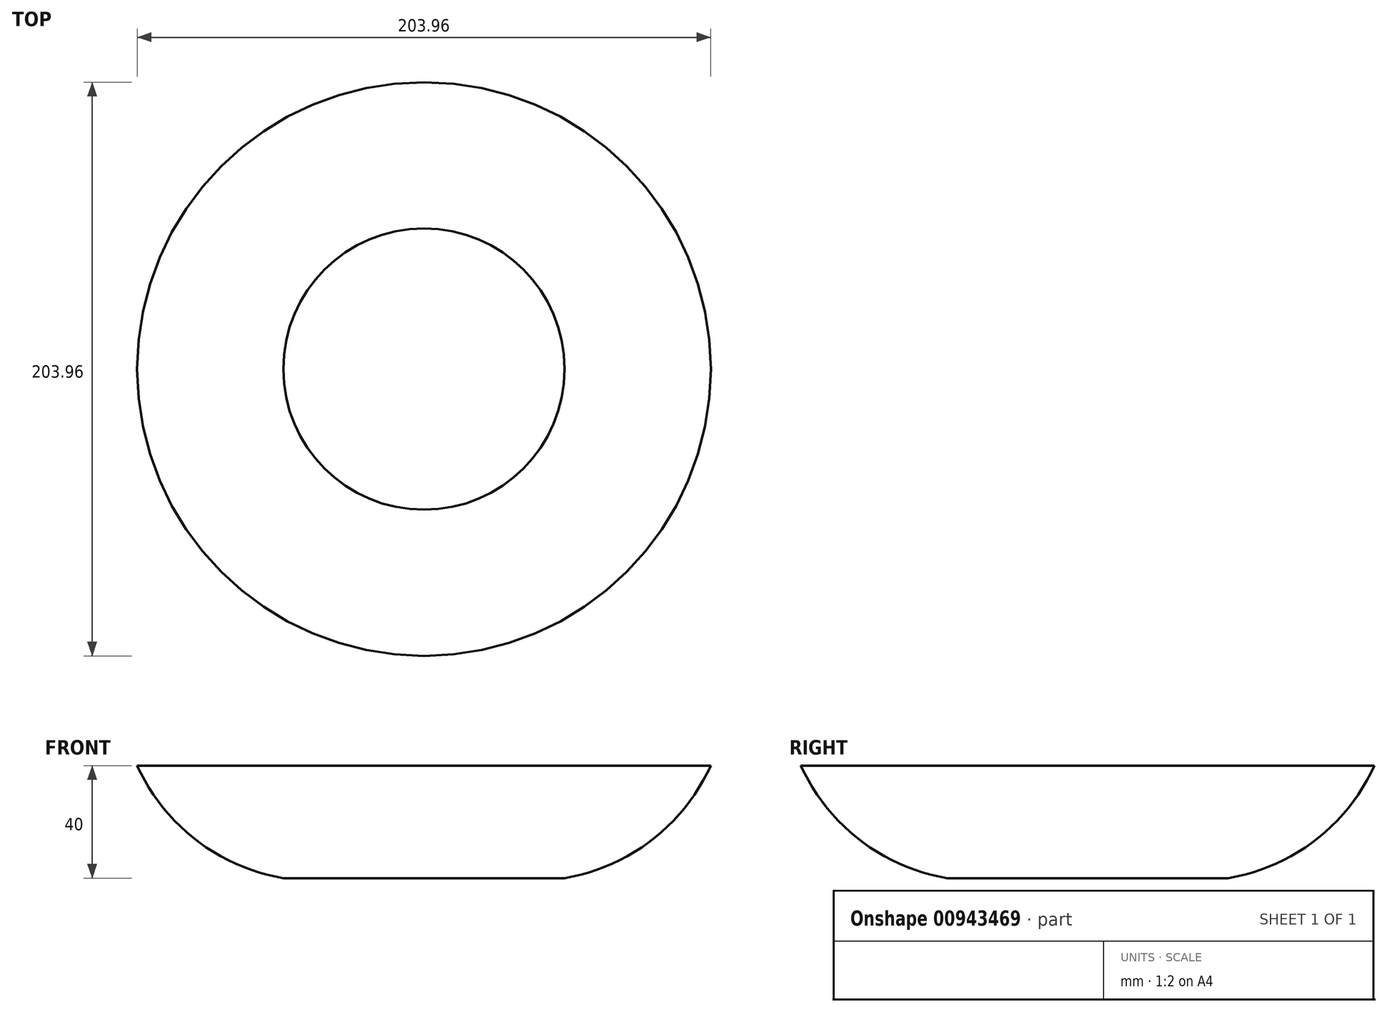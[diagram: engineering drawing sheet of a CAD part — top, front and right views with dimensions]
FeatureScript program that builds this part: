
annotation { "Feature Type Name" : "Feature", "Feature Type Description" : "" }
export const myFeature = defineFeature(function(context is Context, id is Id, definition is map)
    precondition{}
    {
        {
            var Q0;
            Q0=qCreatedBy(makeId("Front.planeOp"),FACE);
            var sketch = newSketch(context, id + "F0", { "sketchPlane" : qUnion([Q0])});
            skLineSegment(sketch, "E0", {"start": v(0, 0) * mm, "end": v(50, 0) * mm});
            skLineSegment(sketch, "E1", {"start": v(0, 0) * mm, "end": v(0, 40) * mm, "construction": true});
            skLineSegment(sketch, "E2", {"start": v(50, 0) * mm, "end": v(150, 0) * mm, "construction": true});
            skArc(sketch, "E3", {"start": v(50, 0) * mm, "mid": v(80.97, 13.53) * mm, "end": v(101.98, 40) * mm});
            skSolve(sketch);
        }
        {
            var Q0;
            Q0=sQuery(id+"F0.wireOp",EDGE,"E3");
            var Q1;
            Q1=sQuery(id+"F0.wireOp",EDGE,"E0");
            var Q2;
            Q2=sQuery(id+"F0.wireOp",EDGE,"E1");
            revolve(context, id + "F1", {"bodyType" : ToolBodyType.SURFACE, "surfaceOperationType" : NewSurfaceOperationType.NEW, "surfaceEntities" : qUnion([Q0, Q1]), "axis" : qUnion([Q2]), "revolveType" : RevolveType.FULL});
        }
    });
